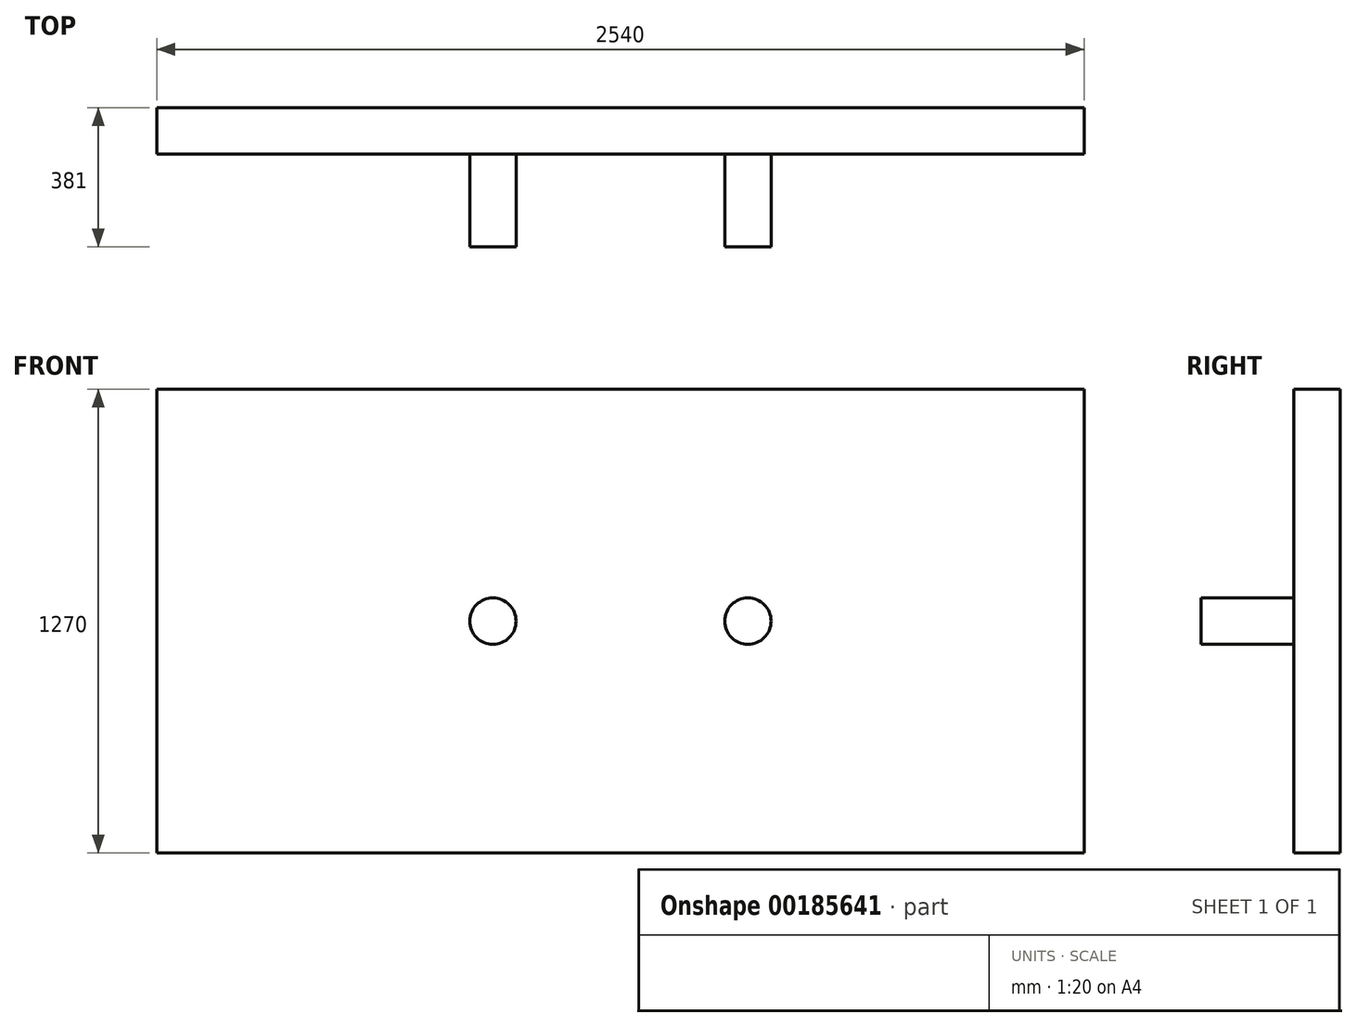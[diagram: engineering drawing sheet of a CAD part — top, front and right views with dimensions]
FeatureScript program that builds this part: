
annotation { "Feature Type Name" : "Feature", "Feature Type Description" : "" }
export const myFeature = defineFeature(function(context is Context, id is Id, definition is map)
    precondition{}
    {
        {
            var Q0;
            Q0=qCreatedBy(makeId("Front.planeOp"),FACE);
            var sketch = newSketch(context, id + "F0", { "sketchPlane" : qUnion([Q0])});
            skLineSegment(sketch, "E0.bottom", {"start": v(1270, 635) * mm, "end": v(-1270, 635) * mm});
            skLineSegment(sketch, "E0.top", {"start": v(1270, -635) * mm, "end": v(-1270, -635) * mm});
            skLineSegment(sketch, "E0.left", {"start": v(1270, 635) * mm, "end": v(1270, -635) * mm});
            skLineSegment(sketch, "E0.right", {"start": v(-1270, 635) * mm, "end": v(-1270, -635) * mm});
            skPoint(sketch, "E0.middle", {"position": v(0, 0) * mm});
            skSolve(sketch);
        }
        {
            var Q0;
            Q0 = qSketchRegion(id + "F0", true);
            extrude(context, id + "F1", {"entities" : qUnion([Q0]), "depth" : 127 * mm});
        }
        {
            var Q0;
            Q0=makeQuery(id+"F1.opExtrude","CAP_FACE",FACE,{"disambiguationData":[OSD([sQuery(id+"F0.wireOp",EDGE,"E0.bottom"),sQuery(id+"F0.wireOp",EDGE,"E0.top"),sQuery(id+"F0.wireOp",EDGE,"E0.left"),sQuery(id+"F0.wireOp",EDGE,"E0.right")])],"isStart":false});
            var sketch = newSketch(context, id + "F2", { "sketchPlane" : qUnion([Q0])});
            skLineSegment(sketch, "E1", {"start": v(0, 0) * mm, "end": v(0, 316.01) * mm, "construction": true});
            skCircle(sketch, "E2", {"center": v(-349.25, 0) * mm, "radius": 63.5 * mm});
            skCircle(sketch, "E3", {"center": v(349.25, 0) * mm, "radius": 63.5 * mm});
            skSolve(sketch);
        }
        {
            var Q0;
            Q0 = qSketchRegion(id + "F2", true);
            extrude(context, id + "F3", {"entities" : qUnion([Q0]), "operationType" : NewBodyOperationType.ADD, "depth" : 254 * mm});
        }
    });
